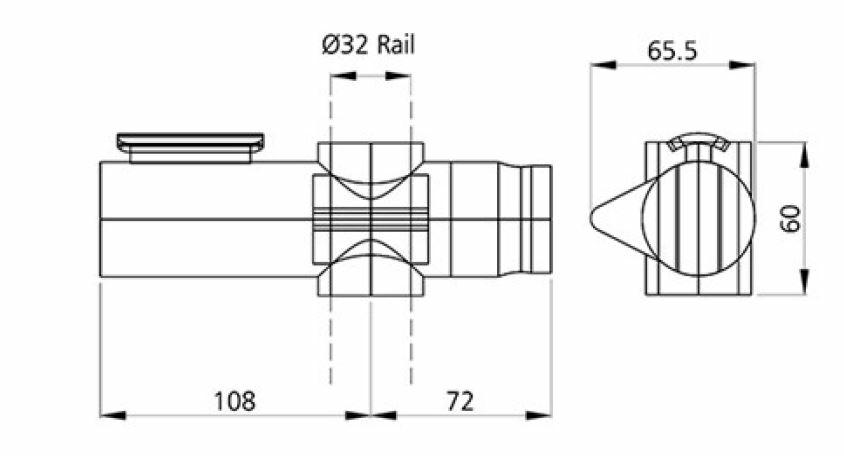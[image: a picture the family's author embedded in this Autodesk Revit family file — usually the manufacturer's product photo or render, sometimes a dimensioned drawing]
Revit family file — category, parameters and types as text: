
# Revit family: RBA4110-994
name_source: partatom
category: Plumbing Fixtures
units: mm (PartAtom-declared; Revit-internal decimal feet)

## family parameters
Always vertical = Yes
Cut with Voids When Loaded = No
Part Type = Normal
Room Calculation Point = No
Round Connector Dimension = Use Diameter
Shared = No
Work Plane-Based = No

## types (1)
- RBA4110-994
    CW Connection = Yes
    Default Elevation = 0 mm  [stored 0 ft]
    Description = Modular Shower Rail & Mixer Kit, Satin Finish
    Distance Away from Toilet (default) = 1090 mm  [stored 3.57612 ft]
    Distance Away from Wall (default) = 100 mm  [stored 0.328084 ft]
    HW Connection = Yes
    Manufacturer = RBA Group
    Materials & Finishes = #304 Stainless Steel, Satin Finish
    Model = RBA4110-994
    OFFSET = 1000 mm  [stored 3.28084 ft]
    URL = www.rba.com.au
    Vent Connection = Yes
    Waste Connection = Yes

note: [stored X ft] marks values corroborated as IEEE doubles in the binary element streams (Revit-internal decimal feet)

## geometry (parser evidence)
native form markers: Blend x8, Sweep x9
no freeform markers — native parametric forms only
